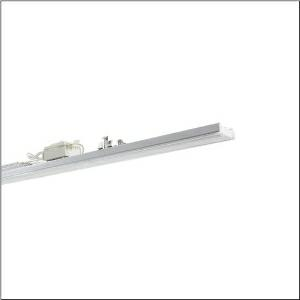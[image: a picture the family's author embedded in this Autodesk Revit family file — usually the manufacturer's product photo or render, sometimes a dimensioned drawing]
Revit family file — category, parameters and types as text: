
# Revit family: licross_11_recessed_extreme_ho_51te12dn4exme
name_source: partatom
category: Lighting Fixtures
units: mm (PartAtom-declared; Revit-internal decimal feet)

## family parameters
Cut with Voids When Loaded = No
Host = Face
Light Source = No
Part Type = Normal
Room Calculation Point = No
Round Connector Dimension = Use Diameter
Shared = No

## types (1)
- --- (1 x LED, 14030 lm, 76.8 W, 4000K)
    Apparent Load = 77 VA
    CIE Flux Codes = 66 91 98 100 100
    Color Rendering = 80
    Color Temperature = 4000K
    Default Elevation = 1800 mm
    Description = Licross 11 Recessed extreme HO, luminaire insert, of sheet steel, galvanised, coil coated, white, length: 1.500mm, width: 66mm, height: 67mm, LED rated luminous flux: 14.030lm, light colour: 840, SDCM (Standard Deviation of Colour Matching)MacAdam ≤ 2 SDCM (initial), control gear: DALI 2, with plug, 5-pole, with phase selection, mains connection: 220..240V, AC, 50/60Hz, rated input power: 77W, internal wiring halogen-free, primary optical cover: cover, of PMMA, light emission: direct distribution, primary light characteristic: symmetric, protection rating (complete): IP54, insulation class (complete): insulation class I (protective earthing), certification: CE, ENEC, VDE, UKCA, protection symbol: D if used in an environment with non-conductive dust loads with corresponding accessories, impact resistance: IK06, permissible ambient temperature for indoor applications: -40..+40°C, corresponds to IFS (International Featured Standards) requirements for safety and quality in the food industry, reducing of maximum allowable ambient temperature of 5°C with ceiling mounting, LABS conformity tested according to VDMA 24364:2018-05, The light source and the operating device comply with the requirements of the Ecodesign Regulation (EU) 2019/2020 and are replaceable in accordance with this regulation, packaging unit: 1 piece
    Height = 58 mm
    Lamp = 1 x LED
    Lamp Light Flux = 14030 lm
    Lamp Power = 76.8 W
    Lamp count = 1
    Length = 1500 mm
    Luminous efficacy = 183 lm/W
    Manufacturer = Siteco
    ModVariant = No
    Model = 51TE12DN4EXME
    Mounting Place = Ceiling
    Mounting Type = Pendant
    Number of Poles = 1
    OnlyDefault = Yes
    Power Factor = 1
    Product Name = Licross 11 Recessed extreme HO
    Product group = luminaire insert | ceiling pendant
    ProductGroupID = 901
    Protection Class = Protection class I
    Protection Degree = IP 54
    RLX_Detail_Level = 1
    RLX_Emergency_Light_Flux = 0 lm
    RLX_Emergency_Type = 0
    RLX_Emergency_Type_DB = No
    RlxData = <blob elided: 24917 chars, md5=3e811b85>
    Socket = socket
    Standby Power = 0 W
    System Light Flux = 14030 lm
    System Power = 77 W
    Type Comments = factory setting: luminous flux: 100 % | dim-lin: 254 | 522 mA
    Type Image = l_1296930.jpg
    URL = http://relux.com
    VarID = @adj_087407
    Voltage = 0 V
    Weight = 0.00 kg
    Width = 66 mm

## geometry (parser evidence)
native form markers: Blend x4, Sweep x11
no freeform markers — native parametric forms only
